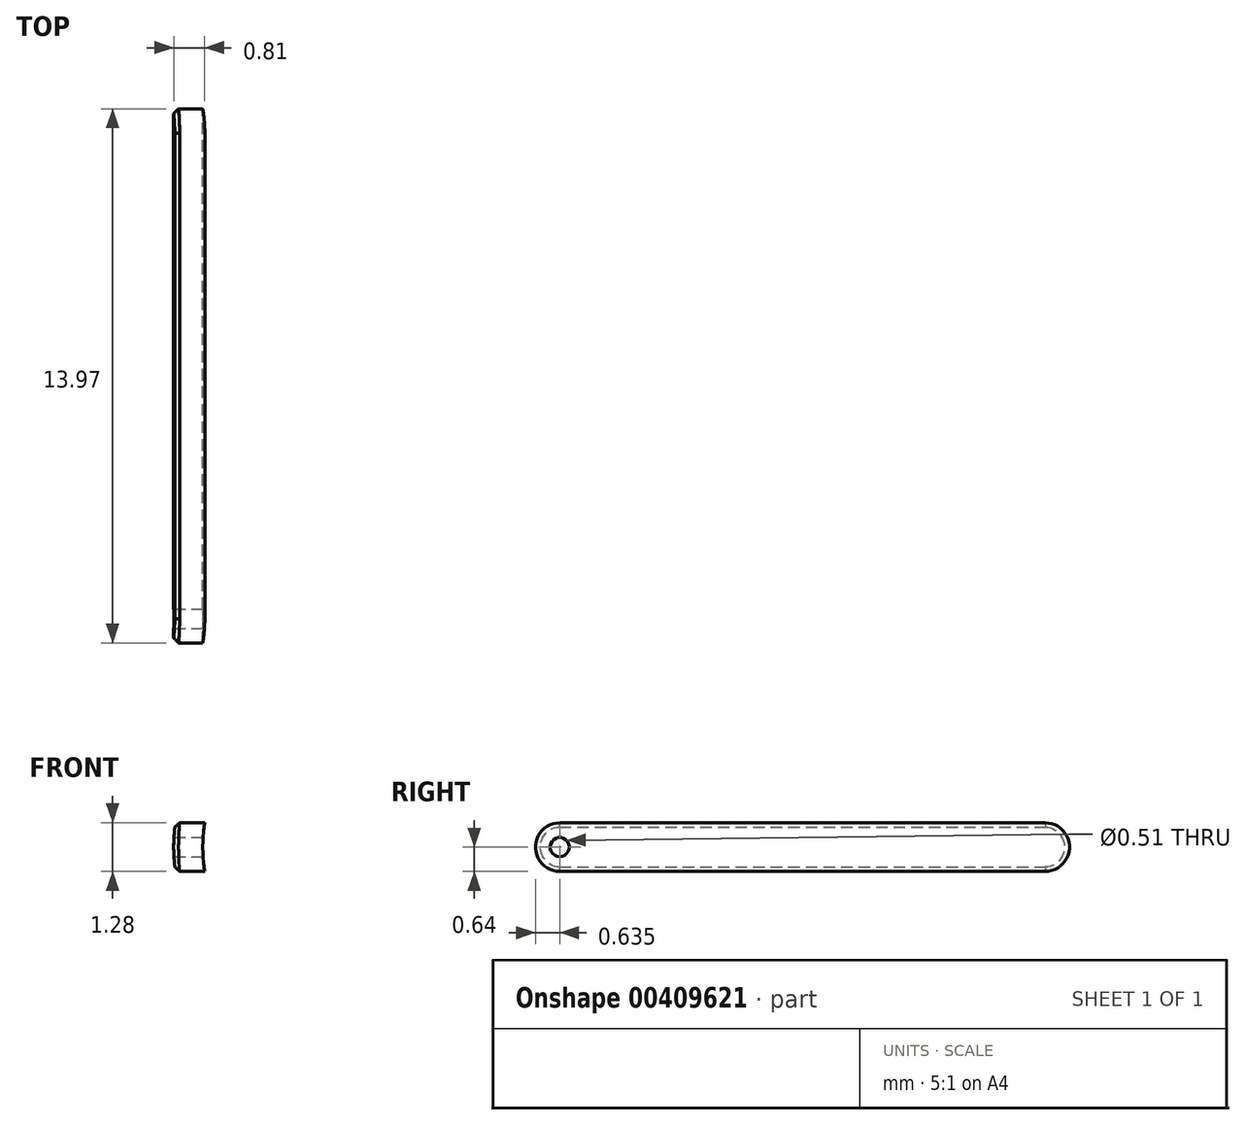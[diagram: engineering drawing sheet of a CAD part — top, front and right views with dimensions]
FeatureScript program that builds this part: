
annotation { "Feature Type Name" : "Feature", "Feature Type Description" : "" }
export const myFeature = defineFeature(function(context is Context, id is Id, definition is map)
    precondition{}
    {
        {
            var Q0;
            Q0=qCreatedBy(makeId("Front.planeOp"),FACE);
            var sketch = newSketch(context, id + "F0", { "sketchPlane" : qUnion([Q0])});
            skArc(sketch, "E0", {"start": v(-3.67, 1.02) * mm, "mid": v(-3.8, 0) * mm, "end": v(-3.67, -1.02) * mm});
            skArc(sketch, "E1.0", {"start": v(-4.46, 1.02) * mm, "mid": v(-4.57, 0) * mm, "end": v(-4.46, -1.02) * mm});
            skLineSegment(sketch, "E2", {"start": v(0, 0) * mm, "end": v(0, 1.02) * mm});
            skLineSegment(sketch, "E3", {"start": v(0, 0) * mm, "end": v(0, -1.02) * mm});
            skLineSegment(sketch, "E4", {"start": v(-3.67, -1.02) * mm, "end": v(-4.46, -1.02) * mm});
            skLineSegment(sketch, "E5", {"start": v(-3.67, 1.02) * mm, "end": v(-4.46, 1.02) * mm});
            skSolve(sketch);
        }
        {
            var Q0;
            Q0 = qSketchRegion(id + "F0", true);
            extrude(context, id + "F1", {"entities" : qUnion([Q0]), "depth" : 25.4 * mm});
        }
        {
            var Q0;
            Q0=qCreatedBy(makeId("Right.planeOp"),FACE);
            var sketch = newSketch(context, id + "F2", { "sketchPlane" : qUnion([Q0])});
            skLineSegment(sketch, "E6", {"start": v(0, 0) * mm, "end": v(-2.54, 0) * mm});
            skArc(sketch, "E7", {"start": v(-3.18, -0.64) * mm, "mid": v(-2.54, 0) * mm, "end": v(-3.18, 0.64) * mm});
            skLineSegment(sketch, "E8", {"start": v(-3.18, -0.64) * mm, "end": v(-15.88, -0.64) * mm});
            skLineSegment(sketch, "E9", {"start": v(-3.18, 0.64) * mm, "end": v(-15.88, 0.64) * mm});
            skArc(sketch, "E10", {"start": v(-15.88, 0.64) * mm, "mid": v(-16.51, 0) * mm, "end": v(-15.88, -0.64) * mm});
            skCircle(sketch, "E11", {"center": v(-15.88, 0) * mm, "radius": 0.25 * mm});
            skLineSegment(sketch, "E12.bottom", {"start": v(10.68, 15.37) * mm, "end": v(-32.3, 15.37) * mm});
            skLineSegment(sketch, "E12.top", {"start": v(10.68, -10.2) * mm, "end": v(-32.3, -10.2) * mm});
            skLineSegment(sketch, "E12.left", {"start": v(10.68, 15.37) * mm, "end": v(10.68, -10.2) * mm});
            skLineSegment(sketch, "E12.right", {"start": v(-32.3, 15.37) * mm, "end": v(-32.3, -10.2) * mm});
            skSolve(sketch);
        }
        {
            var Q0;
            Q0 = qSketchRegion(id + "F2", true);
            var Q1;
            Q1=makeQuery(id+"F2.imprint","IMPRINT",FACE,{"disambiguationData":[TD([[makeQuery(id+"F2.imprint","IMPRINT",EDGE,{"derivedFrom":sQuery(id+"F2.wireOp",EDGE,"E11")}),1.0]])]});
            extrude(context, id + "F3", {"entities" : qUnion([Q0, Q1]), "operationType" : NewBodyOperationType.REMOVE, "oppositeDirection" : true, "depth" : 25.4 * mm});
        }
        {
            var Q0;
            Q0=makeQuery(id+"F3.boolean.opBoolean","INTERSECT",EDGE,{"derivedFrom":[makeQuery(id+"F1.opExtrude","SWEPT_FACE",FACE,{"disambiguationData":[OSD([sQuery(id+"F0.wireOp",EDGE,"E1.0")])]}),makeQuery(id+"F3.opExtrude","SWEPT_FACE",FACE,{"disambiguationData":[OSD([sQuery(id+"F2.wireOp",EDGE,"E8")])]})]});
            chamfer(context, id + "F4", {"entities" : qUnion([Q0]), "width" : 0.13 * mm, "tangentPropagation" : true});
        }
    });
